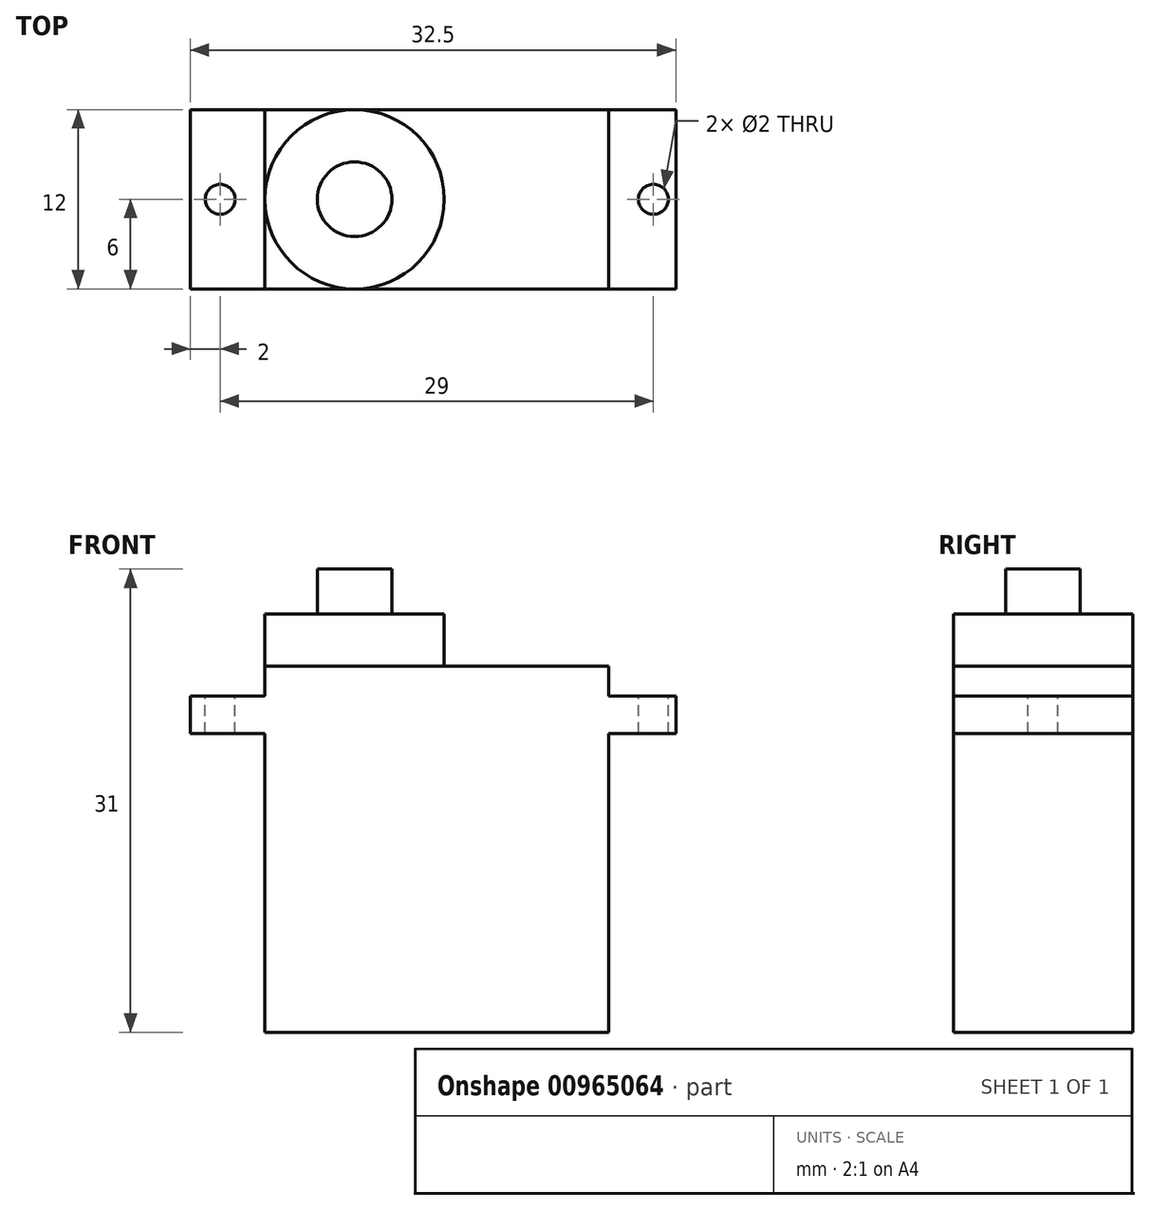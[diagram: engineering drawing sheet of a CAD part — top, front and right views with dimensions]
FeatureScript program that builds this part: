
annotation { "Feature Type Name" : "Feature", "Feature Type Description" : "" }
export const myFeature = defineFeature(function(context is Context, id is Id, definition is map)
    precondition{}
    {
        {
            var Q0;
            Q0=qCreatedBy(makeId("Top.planeOp"),FACE);
            var sketch = newSketch(context, id + "F0", { "sketchPlane" : qUnion([Q0])});
            skLineSegment(sketch, "E0.bottom", {"start": v(0, 0) * mm, "end": v(32.5, 0) * mm});
            skLineSegment(sketch, "E0.top", {"start": v(0, 12) * mm, "end": v(32.5, 12) * mm});
            skLineSegment(sketch, "E0.left", {"start": v(0, 0) * mm, "end": v(0, 12) * mm});
            skLineSegment(sketch, "E0.right", {"start": v(32.5, 0) * mm, "end": v(32.5, 12) * mm});
            skLineSegment(sketch, "E1.bottom", {"start": v(5, 12) * mm, "end": v(28, 12) * mm});
            skLineSegment(sketch, "E1.top", {"start": v(5, 0) * mm, "end": v(28, 0) * mm});
            skLineSegment(sketch, "E1.left", {"start": v(5, 12) * mm, "end": v(5, 0) * mm});
            skLineSegment(sketch, "E1.right", {"start": v(28, 12) * mm, "end": v(28, 0) * mm});
            skCircle(sketch, "E2", {"center": v(2, 6) * mm, "radius": 1 * mm});
            skCircle(sketch, "E3", {"center": v(31, 6) * mm, "radius": 1 * mm});
            skCircle(sketch, "E4", {"center": v(11, 6) * mm, "radius": 6 * mm});
            skCircle(sketch, "E5", {"center": v(11, 6) * mm, "radius": 2.5 * mm});
            skSolve(sketch);
        }
        {
            var Q0;
            {var subQ0=sQuery(id+"F0.wireOp",EDGE,"E0.right");Q0=makeQuery(id+"F0.imprint","IMPRINT",FACE,{"disambiguationData":[TD([[makeQuery(id+"F0.imprint","IMPRINT",EDGE,{"derivedFrom":subQ0}),1.0]])]});}
            var Q1;
            {var subQ0=sQuery(id+"F0.wireOp",EDGE,"E1.right");Q1=makeQuery(id+"F0.imprint","IMPRINT",FACE,{"disambiguationData":[TD([[makeQuery(id+"F0.imprint","IMPRINT",EDGE,{"derivedFrom":subQ0}),-1.0]])]});}
            var Q2;
            {var subQ0=sQuery(id+"F0.wireOp",EDGE,"E4");var subQ1=sQuery(id+"F0.wireOp",EDGE,"E0.top");var subQ2=makeQuery(id+"F0.imprint","INTERSECT",VERTEX,{"derivedFrom":[subQ1,subQ0]});Q2=makeQuery(id+"F0.imprint","IMPRINT",FACE,{"disambiguationData":[TD([[makeQuery(id+"F0.imprint","IMPRINT",EDGE,{"disambiguationData":[TD([[subQ2,1.0]])],"derivedFrom":subQ1}),-1.0]])]});}
            var Q3;
            {var subQ0=sQuery(id+"F0.wireOp",EDGE,"E4");var subQ1=sQuery(id+"F0.wireOp",EDGE,"E0.bottom");var subQ2=makeQuery(id+"F0.imprint","INTERSECT",VERTEX,{"derivedFrom":[subQ1,subQ0]});Q3=makeQuery(id+"F0.imprint","IMPRINT",FACE,{"disambiguationData":[TD([[makeQuery(id+"F0.imprint","IMPRINT",EDGE,{"disambiguationData":[TD([[subQ2,1.0]])],"derivedFrom":subQ1}),1.0]])]});}
            var Q4;
            {var subQ4=sQuery(id+"F0.wireOp",EDGE,"E0.left");Q4=makeQuery(id+"F0.imprint","IMPRINT",FACE,{"disambiguationData":[TD([[makeQuery(id+"F0.imprint","IMPRINT",EDGE,{"derivedFrom":subQ4}),-1.0]])]});}
            var Q5;
            Q5=makeQuery(id+"F0.imprint","IMPRINT",FACE,{"disambiguationData":[TD([[makeQuery(id+"F0.imprint","IMPRINT",EDGE,{"derivedFrom":sQuery(id+"F0.wireOp",EDGE,"E5")}),-1.0]])]});
            var Q6;
            Q6=makeQuery(id+"F0.imprint","IMPRINT",FACE,{"disambiguationData":[TD([[makeQuery(id+"F0.imprint","IMPRINT",EDGE,{"derivedFrom":sQuery(id+"F0.wireOp",EDGE,"E5")}),1.0]])]});
            extrude(context, id + "F1", {"entities" : qUnion([Q0, Q1, Q2, Q3, Q4, Q5, Q6]), "oppositeDirection" : true, "depth" : 2.5 * mm, "offsetDistance" : 25 * mm});
        }
        {
            var Q0;
            {var subQ0=sQuery(id+"F0.wireOp",EDGE,"E1.right");Q0=makeQuery(id+"F0.imprint","IMPRINT",FACE,{"disambiguationData":[TD([[makeQuery(id+"F0.imprint","IMPRINT",EDGE,{"derivedFrom":subQ0}),-1.0]])]});}
            var Q1;
            {var subQ0=sQuery(id+"F0.wireOp",EDGE,"E4");var subQ1=sQuery(id+"F0.wireOp",EDGE,"E0.top");var subQ2=makeQuery(id+"F0.imprint","INTERSECT",VERTEX,{"derivedFrom":[subQ1,subQ0]});Q1=makeQuery(id+"F0.imprint","IMPRINT",FACE,{"disambiguationData":[TD([[makeQuery(id+"F0.imprint","IMPRINT",EDGE,{"disambiguationData":[TD([[subQ2,1.0]])],"derivedFrom":subQ1}),-1.0]])]});}
            var Q2;
            {var subQ0=sQuery(id+"F0.wireOp",EDGE,"E4");var subQ1=sQuery(id+"F0.wireOp",EDGE,"E0.bottom");var subQ2=makeQuery(id+"F0.imprint","INTERSECT",VERTEX,{"derivedFrom":[subQ1,subQ0]});Q2=makeQuery(id+"F0.imprint","IMPRINT",FACE,{"disambiguationData":[TD([[makeQuery(id+"F0.imprint","IMPRINT",EDGE,{"disambiguationData":[TD([[subQ2,1.0]])],"derivedFrom":subQ1}),1.0]])]});}
            var Q3;
            Q3=makeQuery(id+"F0.imprint","IMPRINT",FACE,{"disambiguationData":[TD([[makeQuery(id+"F0.imprint","IMPRINT",EDGE,{"derivedFrom":sQuery(id+"F0.wireOp",EDGE,"E5")}),-1.0]])]});
            var Q4;
            Q4=makeQuery(id+"F0.imprint","IMPRINT",FACE,{"disambiguationData":[TD([[makeQuery(id+"F0.imprint","IMPRINT",EDGE,{"derivedFrom":sQuery(id+"F0.wireOp",EDGE,"E5")}),1.0]])]});
            extrude(context, id + "F2", {"entities" : qUnion([Q0, Q1, Q2, Q3, Q4]), "operationType" : NewBodyOperationType.ADD, "depth" : 2 * mm, "offsetDistance" : 25 * mm});
        }
        {
            var Q0;
            {var subQ0=sQuery(id+"F0.wireOp",EDGE,"E1.right");Q0=makeQuery(id+"F0.imprint","IMPRINT",FACE,{"disambiguationData":[TD([[makeQuery(id+"F0.imprint","IMPRINT",EDGE,{"derivedFrom":subQ0}),-1.0]])]});}
            var Q1;
            Q1=makeQuery(id+"F0.imprint","IMPRINT",FACE,{"disambiguationData":[TD([[makeQuery(id+"F0.imprint","IMPRINT",EDGE,{"derivedFrom":sQuery(id+"F0.wireOp",EDGE,"E5")}),-1.0]])]});
            var Q2;
            Q2=makeQuery(id+"F0.imprint","IMPRINT",FACE,{"disambiguationData":[TD([[makeQuery(id+"F0.imprint","IMPRINT",EDGE,{"derivedFrom":sQuery(id+"F0.wireOp",EDGE,"E5")}),1.0]])]});
            var Q3;
            {var subQ0=sQuery(id+"F0.wireOp",EDGE,"E4");var subQ1=sQuery(id+"F0.wireOp",EDGE,"E0.top");var subQ2=makeQuery(id+"F0.imprint","INTERSECT",VERTEX,{"derivedFrom":[subQ1,subQ0]});Q3=makeQuery(id+"F0.imprint","IMPRINT",FACE,{"disambiguationData":[TD([[makeQuery(id+"F0.imprint","IMPRINT",EDGE,{"disambiguationData":[TD([[subQ2,1.0]])],"derivedFrom":subQ1}),-1.0]])]});}
            var Q4;
            {var subQ0=sQuery(id+"F0.wireOp",EDGE,"E4");var subQ1=sQuery(id+"F0.wireOp",EDGE,"E0.bottom");var subQ2=makeQuery(id+"F0.imprint","INTERSECT",VERTEX,{"derivedFrom":[subQ1,subQ0]});Q4=makeQuery(id+"F0.imprint","IMPRINT",FACE,{"disambiguationData":[TD([[makeQuery(id+"F0.imprint","IMPRINT",EDGE,{"disambiguationData":[TD([[subQ2,1.0]])],"derivedFrom":subQ1}),1.0]])]});}
            extrude(context, id + "F3", {"entities" : qUnion([Q0, Q1, Q2, Q3, Q4]), "oppositeDirection" : true, "depth" : 22.5 * mm, "offsetDistance" : 25 * mm});
        }
        {
            var Q0;
            Q0=makeQuery(id+"F2.opExtrude","CAP_FACE",FACE,{"disambiguationData":[OSD([sQuery(id+"F0.wireOp",EDGE,"E0.bottom"),sQuery(id+"F0.wireOp",EDGE,"E0.top"),sQuery(id+"F0.wireOp",EDGE,"E1.left"),sQuery(id+"F0.wireOp",EDGE,"E1.right")])],"isStart":false});
            var sketch = newSketch(context, id + "F4", { "sketchPlane" : qUnion([Q0])});
            skCircle(sketch, "E6", {"center": v(11, 6) * mm, "radius": 6 * mm});
            skCircle(sketch, "E7", {"center": v(11, 6) * mm, "radius": 2.5 * mm});
            skSolve(sketch);
        }
        {
            var Q0;
            Q0=makeQuery(id+"F4.imprint","IMPRINT",FACE,{"disambiguationData":[TD([[makeQuery(id+"F4.imprint","IMPRINT",EDGE,{"derivedFrom":sQuery(id+"F4.wireOp",EDGE,"E7")}),-1.0]])]});
            extrude(context, id + "F5", {"entities" : qUnion([Q0]), "operationType" : NewBodyOperationType.ADD, "depth" : 3.5 * mm, "offsetDistance" : 25 * mm});
        }
        {
            var Q0;
            Q0=makeQuery(id+"F5.boolean.opBoolean","SPLIT",FACE,{"disambiguationData":[TD([makeQuery(id+"F5.opExtrude","SWEPT_FACE",FACE,{"disambiguationData":[OSD([sQuery(id+"F4.wireOp",EDGE,"E7")])]})])],"derivedFrom":makeQuery(id+"F2.opExtrude","CAP_FACE",FACE,{"disambiguationData":[OSD([sQuery(id+"F0.wireOp",EDGE,"E0.bottom"),sQuery(id+"F0.wireOp",EDGE,"E0.top"),sQuery(id+"F0.wireOp",EDGE,"E1.left"),sQuery(id+"F0.wireOp",EDGE,"E1.right")])],"isStart":false})});
            extrude(context, id + "F6", {"entities" : qUnion([Q0]), "operationType" : NewBodyOperationType.ADD, "depth" : 6.5 * mm, "offsetDistance" : 25 * mm});
        }
        {
            var Q0;
            Q0=makeQuery(id+"F3.opExtrude","SWEPT_BODY",BODY,{"disambiguationData":[OSD([sQuery(id+"F0.wireOp",EDGE,"E0.bottom"),sQuery(id+"F0.wireOp",EDGE,"E0.top"),sQuery(id+"F0.wireOp",EDGE,"E1.left"),sQuery(id+"F0.wireOp",EDGE,"E1.right")])]});
            deleteBodies(context, id + "F7", {"entities" : qUnion([Q0])});
        }
        {
            var Q0;
            Q0=makeQuery(id+"F1.opExtrude","CAP_FACE",FACE,{"disambiguationData":[OSD([sQuery(id+"F0.wireOp",EDGE,"E0.bottom"),sQuery(id+"F0.wireOp",EDGE,"E0.top"),sQuery(id+"F0.wireOp",EDGE,"E0.left"),sQuery(id+"F0.wireOp",EDGE,"E0.right"),sQuery(id+"F0.wireOp",EDGE,"E2"),sQuery(id+"F0.wireOp",EDGE,"E3")])],"isStart":false});
            var sketch = newSketch(context, id + "F8", { "sketchPlane" : qUnion([Q0])});
            skLineSegment(sketch, "E8.bottom", {"start": v(5, 0) * mm, "end": v(28, 0) * mm});
            skLineSegment(sketch, "E8.top", {"start": v(5, -12) * mm, "end": v(28, -12) * mm});
            skLineSegment(sketch, "E8.left", {"start": v(5, 0) * mm, "end": v(5, -12) * mm});
            skLineSegment(sketch, "E8.right", {"start": v(28, 0) * mm, "end": v(28, -12) * mm});
            skSolve(sketch);
        }
        {
            var Q0;
            Q0=makeQuery(id+"F8.imprint","IMPRINT",FACE,{"disambiguationData":[TD([[makeQuery(id+"F8.imprint","IMPRINT",EDGE,{"derivedFrom":sQuery(id+"F8.wireOp",EDGE,"E8.bottom")}),-1.0]])]});
            extrude(context, id + "F9", {"entities" : qUnion([Q0]), "operationType" : NewBodyOperationType.ADD, "depth" : 20 * mm, "offsetDistance" : 25 * mm});
        }
    });
